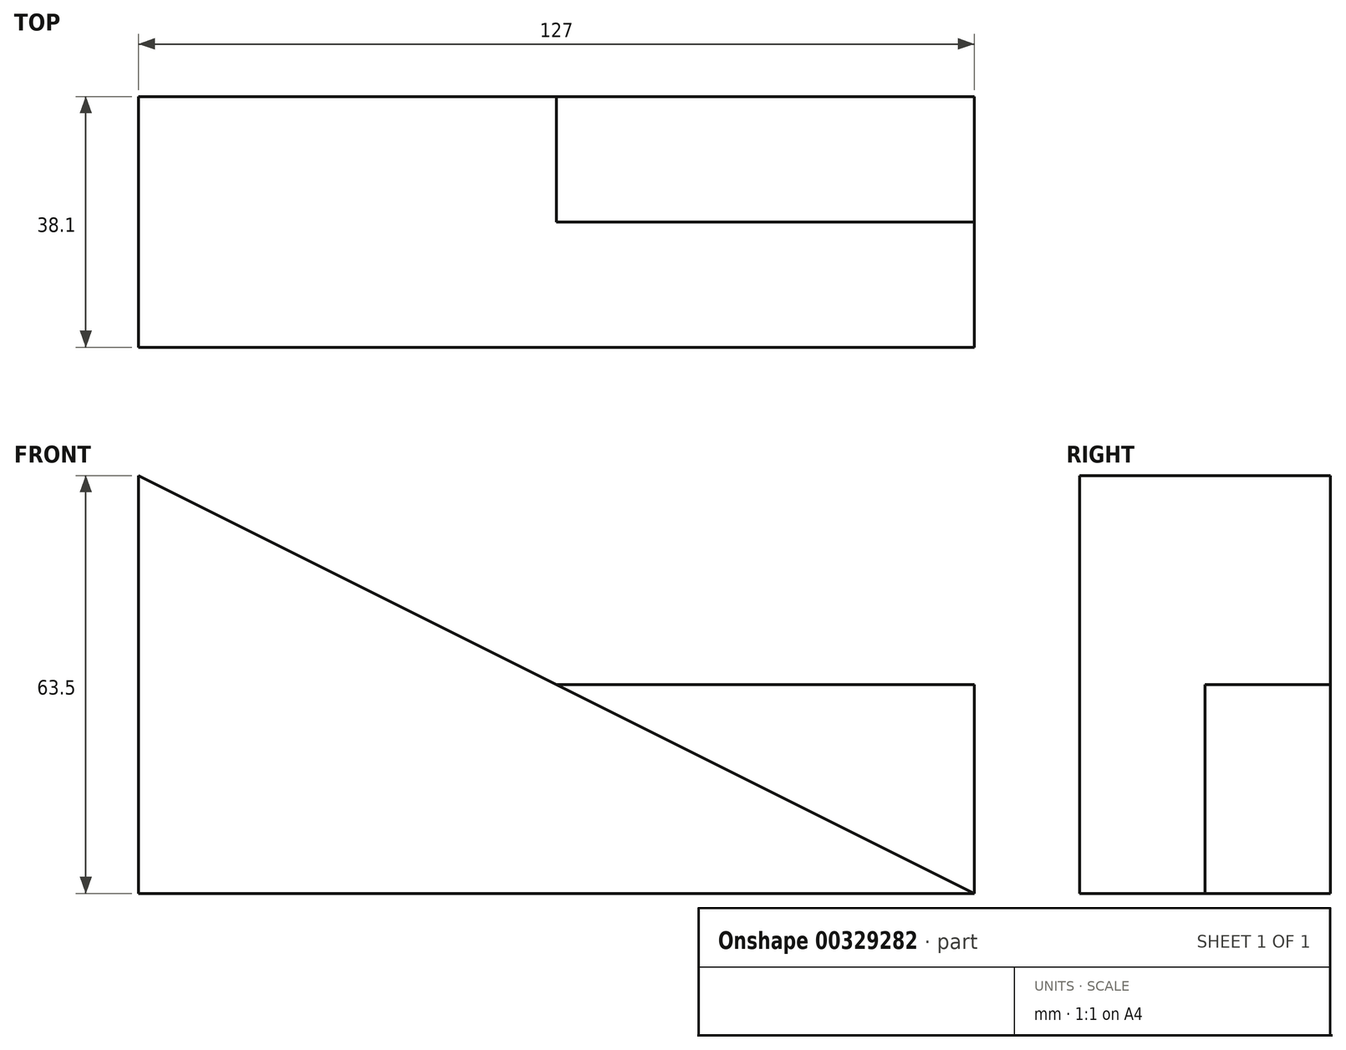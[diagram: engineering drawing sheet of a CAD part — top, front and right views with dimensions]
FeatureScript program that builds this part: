
annotation { "Feature Type Name" : "Feature", "Feature Type Description" : "" }
export const myFeature = defineFeature(function(context is Context, id is Id, definition is map)
    precondition{}
    {
        {
            var Q0;
            Q0=qCreatedBy(makeId("Front.planeOp"),FACE);
            var sketch = newSketch(context, id + "F0", { "sketchPlane" : qUnion([Q0])});
            skLineSegment(sketch, "E0", {"start": v(-58.54, -24.63) * mm, "end": v(68.46, -24.63) * mm});
            skLineSegment(sketch, "E1", {"start": v(-58.54, -24.63) * mm, "end": v(-58.54, 38.87) * mm});
            skLineSegment(sketch, "E2", {"start": v(-58.54, 38.87) * mm, "end": v(68.46, -24.63) * mm});
            skLineSegment(sketch, "E3", {"start": v(68.46, -24.63) * mm, "end": v(68.46, 7.12) * mm});
            skPoint(sketch, "E4.end.orphan", {"position": v(4.96, 7.12) * mm});
            skLineSegment(sketch, "E5", {"start": v(68.46, 7.12) * mm, "end": v(4.96, 7.12) * mm});
            skSolve(sketch);
        }
        {
            var Q0;
            {var subQ0=sQuery(id+"F0.wireOp",EDGE,"E0");Q0=makeQuery(id+"F0.imprint","IMPRINT",FACE,{"disambiguationData":[TD([[makeQuery(id+"F0.imprint","IMPRINT",EDGE,{"derivedFrom":subQ0}),1.0]])]});}
            extrude(context, id + "F1", {"entities" : qUnion([Q0]), "depth" : 38.1 * mm});
        }
        {
            var Q0;
            Q0 = qSketchRegion(id + "F0", true);
            extrude(context, id + "F2", {"entities" : qUnion([Q0]), "operationType" : NewBodyOperationType.ADD, "depth" : 19.05 * mm});
        }
    });
